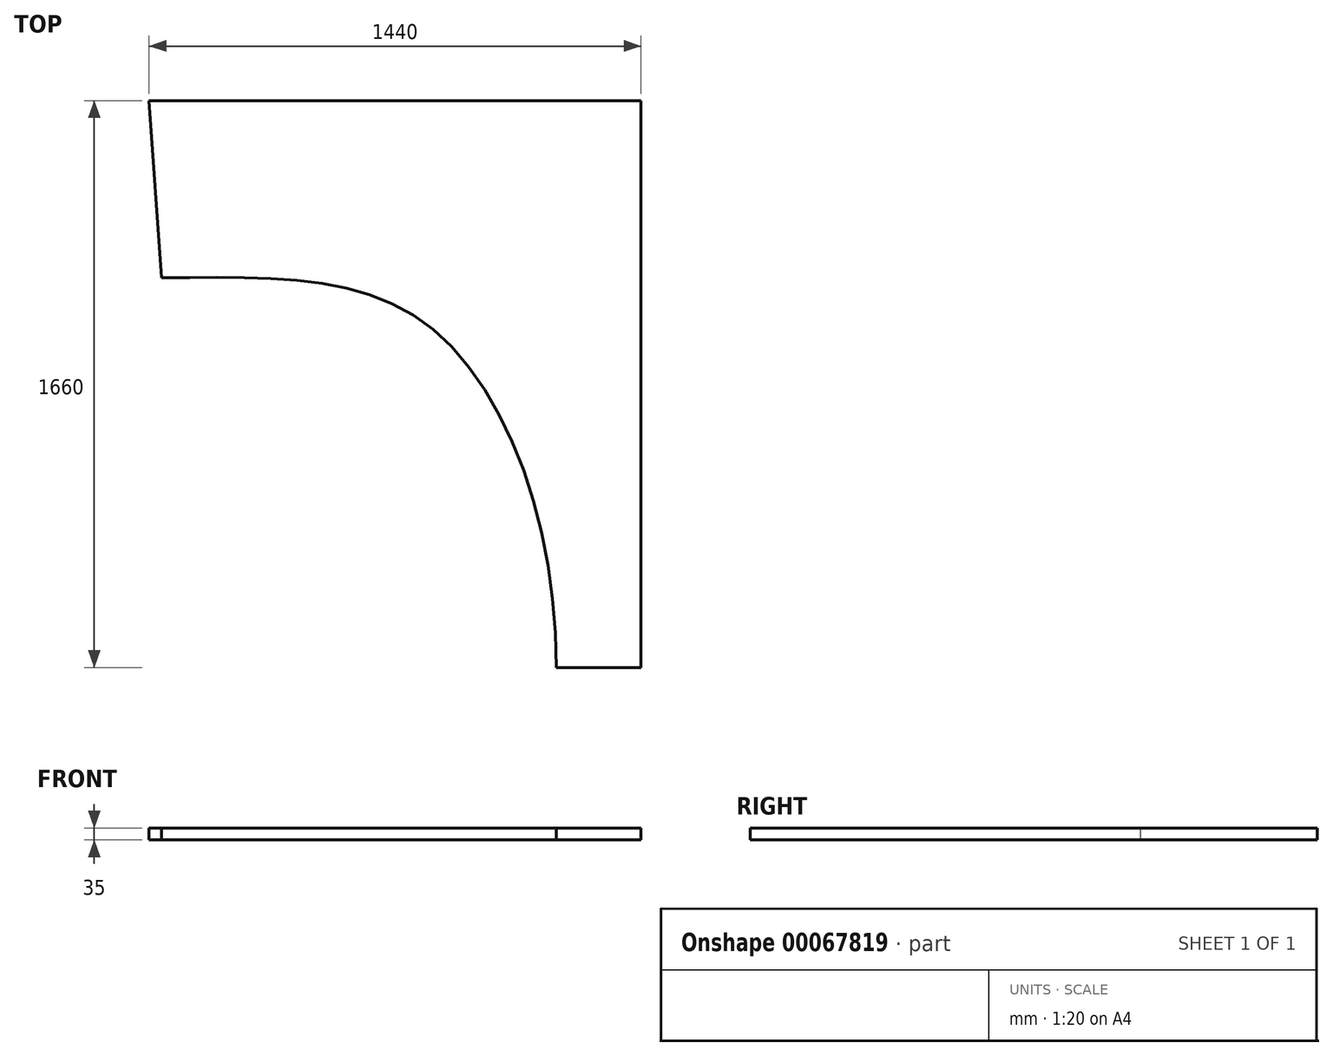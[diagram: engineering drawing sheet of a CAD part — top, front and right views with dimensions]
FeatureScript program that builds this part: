
annotation { "Feature Type Name" : "Feature", "Feature Type Description" : "" }
export const myFeature = defineFeature(function(context is Context, id is Id, definition is map)
    precondition{}
    {
        {
            var Q0;
            Q0=qCreatedBy(makeId("Top.planeOp"),FACE);
            var sketch = newSketch(context, id + "F0", { "sketchPlane" : qUnion([Q0])});
            skLineSegment(sketch, "E0.top", {"start": v(0, 1660) * mm, "end": v(1440, 1660) * mm});
            skLineSegment(sketch, "E0.right", {"start": v(1440, 0) * mm, "end": v(1440, 1660) * mm});
            skLineSegment(sketch, "E1", {"start": v(0, 1660) * mm, "end": v(36.5, 1141.35) * mm, "construction": true});
            skSolve(sketch);
        }
        {
            var Q0;
            Q0=qCreatedBy(makeId("Top.planeOp"),FACE);
            var sketch = newSketch(context, id + "F1", { "sketchPlane" : qUnion([Q0])});
            skLineSegment(sketch, "E2.0", {"start": v(0, 1660) * mm, "end": v(36.5, 1141.35) * mm});
            skLineSegment(sketch, "E3.0", {"start": v(0, 1660) * mm, "end": v(1440, 1660) * mm});
            skLineSegment(sketch, "E4.0", {"start": v(1440, 0) * mm, "end": v(1440, 1660) * mm});
            skFitSpline(sketch, "E5", {"points": [v(36.5, 1141.35) * mm, v(806.53, 1008.93) * mm, v(1192.21, 0) * mm], "startDerivative": vector(1897.86, 0) * mm, "endDerivative": vector(0, -2338.12) * mm});
            skLineSegment(sketch, "E6", {"start": v(1192.21, 0) * mm, "end": v(1192.21, -191.4) * mm, "construction": true});
            skLineSegment(sketch, "E7", {"start": v(1192.21, 0) * mm, "end": v(1440, 0) * mm});
            skLineSegment(sketch, "E8", {"start": v(36.5, 1141.35) * mm, "end": v(-418.74, 1141.35) * mm, "construction": true});
            skSolve(sketch);
        }
        {
            var Q0;
            Q0=makeQuery(id+"F1.imprint","IMPRINT",FACE,{"disambiguationData":[TD([[makeQuery(id+"F1.imprint","IMPRINT",EDGE,{"derivedFrom":sQuery(id+"F1.wireOp",EDGE,"E2.0")}),1.0]])]});
            extrude(context, id + "F2", {"entities" : qUnion([Q0]), "depth" : 35 * mm});
        }
    });
